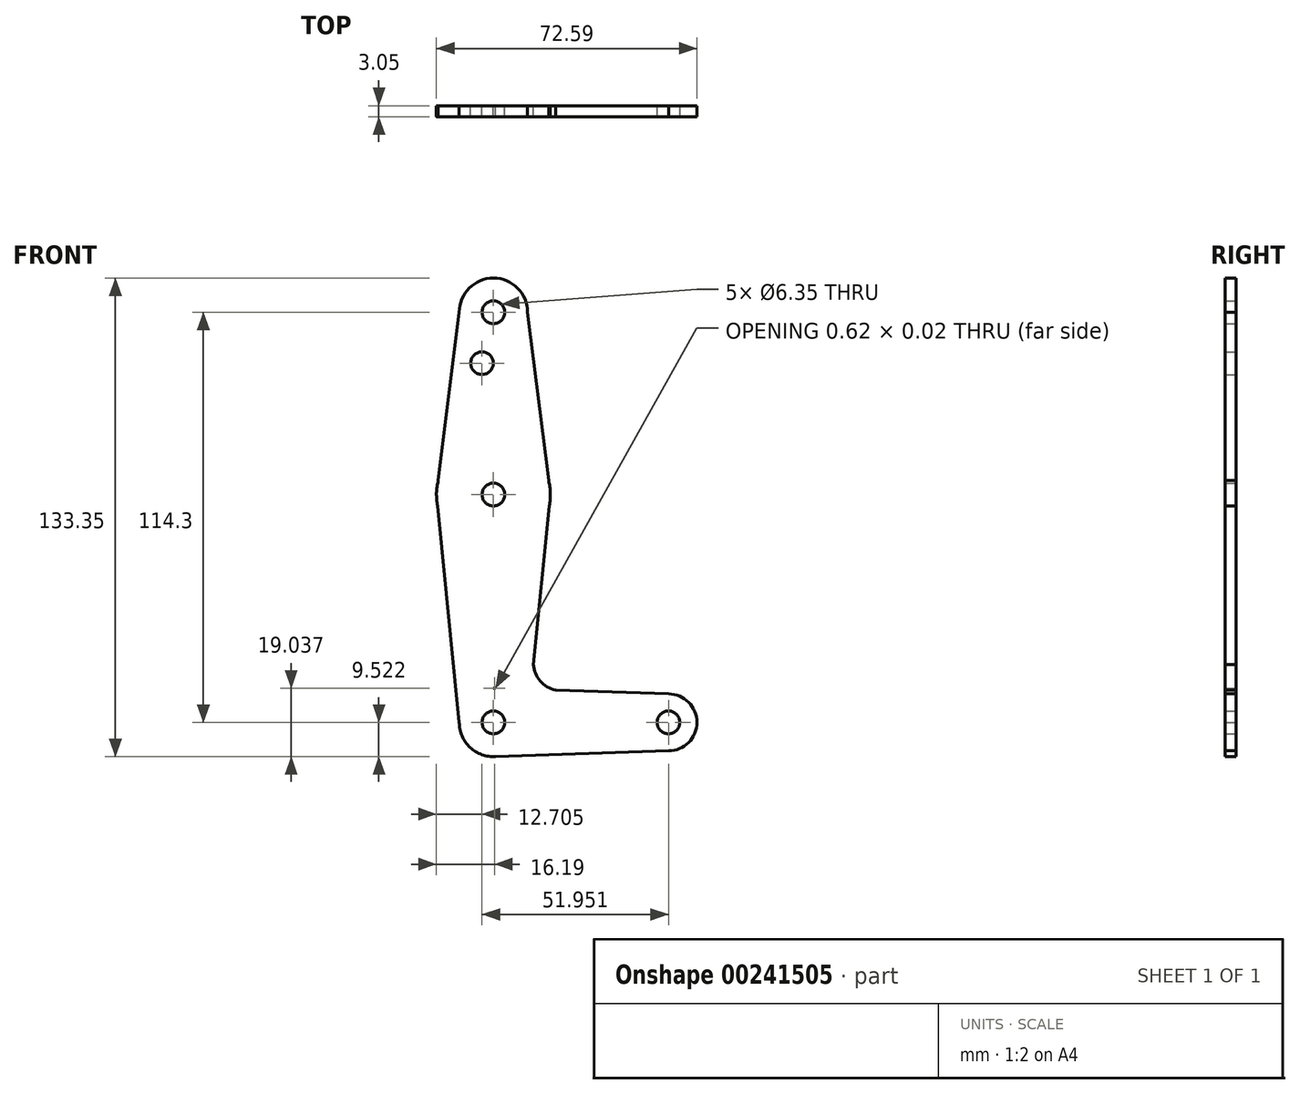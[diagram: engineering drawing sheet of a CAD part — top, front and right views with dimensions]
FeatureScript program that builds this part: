
annotation { "Feature Type Name" : "Feature", "Feature Type Description" : "" }
export const myFeature = defineFeature(function(context is Context, id is Id, definition is map)
    precondition{}
    {
        {
            var Q0;
            Q0=qCreatedBy(makeId("Front.planeOp"),FACE);
            var sketch = newSketch(context, id + "F0", { "sketchPlane" : qUnion([Q0])});
            skCircle(sketch, "E0", {"center": v(0, 66.52) * mm, "radius": 9.53 * mm});
            skCircle(sketch, "E1", {"center": v(0, 66.52) * mm, "radius": 3.18 * mm});
            skCircle(sketch, "E2", {"center": v(0, -47.78) * mm, "radius": 9.53 * mm});
            skCircle(sketch, "E3", {"center": v(0, -47.78) * mm, "radius": 3.18 * mm});
            skCircle(sketch, "E4", {"center": v(0, 15.72) * mm, "radius": 15.88 * mm});
            skCircle(sketch, "E5", {"center": v(0, 15.72) * mm, "radius": 3.18 * mm});
            skCircle(sketch, "E6", {"center": v(48.78, -47.78) * mm, "radius": 7.94 * mm});
            skCircle(sketch, "E7", {"center": v(48.78, -47.78) * mm, "radius": 3.18 * mm});
            skLineSegment(sketch, "E8", {"start": v(-15.88, 15.72) * mm, "end": v(-9.52, -47.78) * mm});
            skLineSegment(sketch, "E9", {"start": v(-15.88, 15.72) * mm, "end": v(-9.53, 66.52) * mm});
            skLineSegment(sketch, "E10", {"start": v(9.52, 66.52) * mm, "end": v(15.88, 15.72) * mm});
            skLineSegment(sketch, "E11", {"start": v(15.88, 15.72) * mm, "end": v(9.52, -47.78) * mm});
            skLineSegment(sketch, "E12", {"start": v(0, -57.3) * mm, "end": v(48.78, -55.72) * mm});
            skLineSegment(sketch, "E13", {"start": v(48.78, -39.84) * mm, "end": v(0, -38.25) * mm});
            skCircle(sketch, "E14", {"center": v(-3.18, 52.34) * mm, "radius": 3.18 * mm});
            skArc(sketch, "E15", {"start": v(11.41, -28.92) * mm, "mid": v(13.12, -36.32) * mm, "end": v(20.26, -38.91) * mm});
            skSolve(sketch);
        }
        {
            var Q0;
            Q0 = qSketchRegion(id + "F0", true);
            var Q1;
            {var subQ0=sQuery(id+"F0.wireOp",EDGE,"E11");var subQ1=sQuery(id+"F0.wireOp",EDGE,"E2");var subQ2=makeQuery(id+"F0.imprint","INTERSECT",VERTEX,{"derivedFrom":[subQ1,subQ0]});Q1=makeQuery(id+"F0.imprint","IMPRINT",FACE,{"disambiguationData":[TD([[makeQuery(id+"F0.imprint","IMPRINT",EDGE,{"disambiguationData":[TD([[subQ2,-1.0]])],"derivedFrom":subQ1}),-1.0]])]});}
            extrude(context, id + "F1", {"entities" : qUnion([Q0, Q1]), "depth" : 3.05 * mm});
        }
    });
